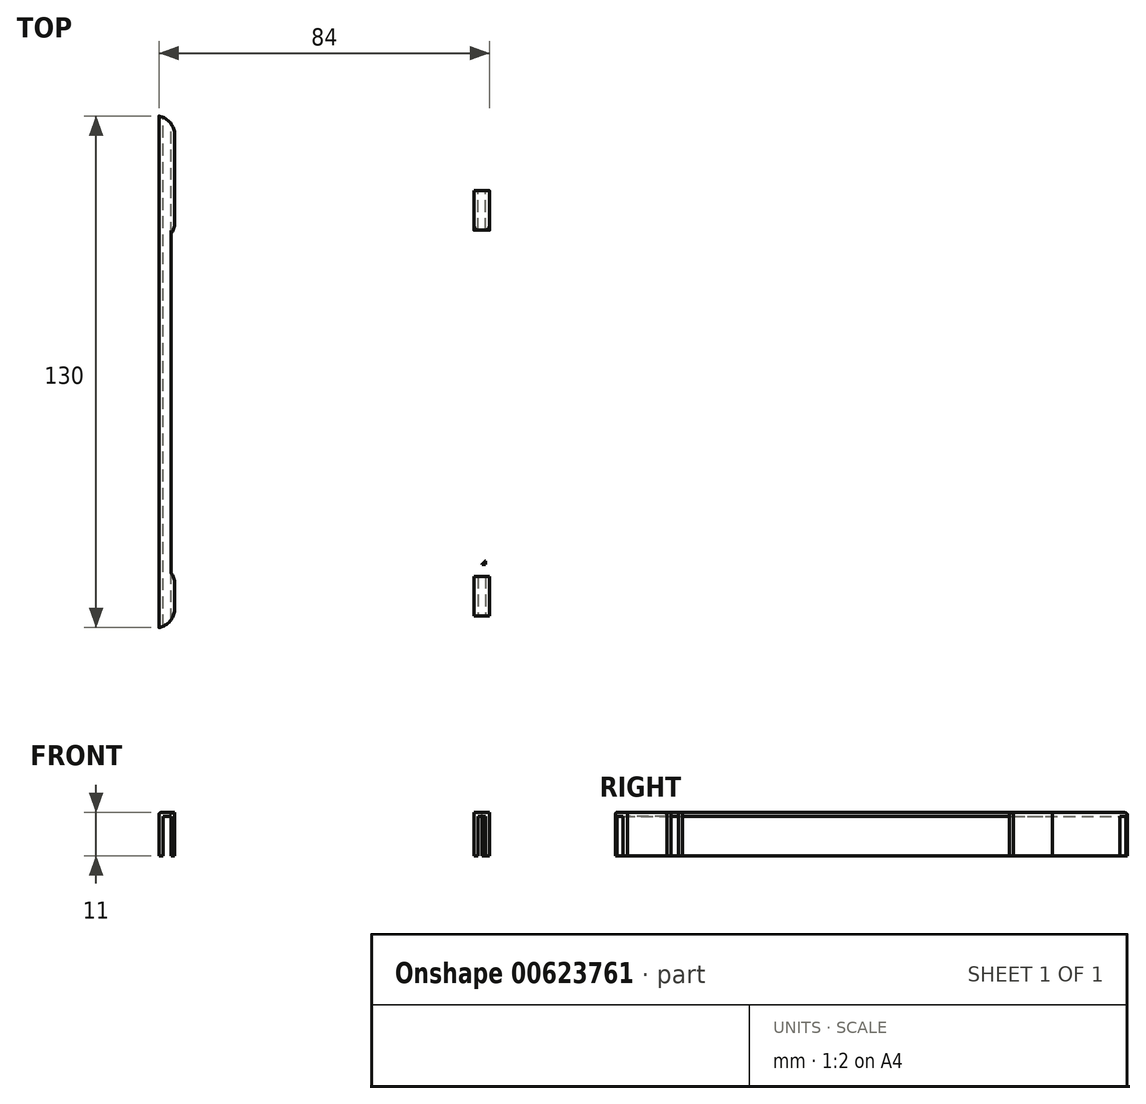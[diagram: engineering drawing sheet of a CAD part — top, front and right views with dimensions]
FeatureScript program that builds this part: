
annotation { "Feature Type Name" : "Feature", "Feature Type Description" : "" }
export const myFeature = defineFeature(function(context is Context, id is Id, definition is map)
    precondition{}
    {
        {
            var Q0;
            Q0=qCreatedBy(makeId("Top.planeOp"),FACE);
            var sketch = newSketch(context, id + "F0", { "sketchPlane" : qUnion([Q0])});
            skLineSegment(sketch, "E0.bottom", {"start": v(1, -65) * mm, "end": v(-1, -65) * mm});
            skLineSegment(sketch, "E0.top", {"start": v(1, 65) * mm, "end": v(-1, 65) * mm});
            skLineSegment(sketch, "E0.left", {"start": v(1, -65) * mm, "end": v(1, 65) * mm});
            skLineSegment(sketch, "E0.right", {"start": v(-1, -65) * mm, "end": v(-1, 65) * mm});
            skPoint(sketch, "E0.middle", {"position": v(0, 0) * mm});
            skLineSegment(sketch, "E1.bottom", {"start": v(1, -49) * mm, "end": v(120, -49) * mm});
            skLineSegment(sketch, "E1.top", {"start": v(1, -51) * mm, "end": v(120, -51) * mm});
            skLineSegment(sketch, "E1.left", {"start": v(1, -49) * mm, "end": v(1, -51) * mm});
            skLineSegment(sketch, "E1.right", {"start": v(120, -49) * mm, "end": v(120, -51) * mm});
            skLineSegment(sketch, "E2", {"start": v(1, -65) * mm, "end": v(1, -51) * mm});
            skLineSegment(sketch, "E3.bottom", {"start": v(1, 35) * mm, "end": v(120, 35) * mm});
            skLineSegment(sketch, "E3.top", {"start": v(1, 33) * mm, "end": v(120, 33) * mm});
            skLineSegment(sketch, "E3.left", {"start": v(1, 35) * mm, "end": v(1, 33) * mm});
            skLineSegment(sketch, "E3.right", {"start": v(120, 35) * mm, "end": v(120, 33) * mm});
            skLineSegment(sketch, "E4", {"start": v(1, 33) * mm, "end": v(1, -49) * mm});
            skLineSegment(sketch, "E5.bottom", {"start": v(-1, 65) * mm, "end": v(-2, 65) * mm});
            skLineSegment(sketch, "E5.top", {"start": v(-1, -65) * mm, "end": v(-2, -65) * mm});
            skLineSegment(sketch, "E5.left", {"start": v(-1, 65) * mm, "end": v(-1, -65) * mm});
            skLineSegment(sketch, "E5.right", {"start": v(-2, 65) * mm, "end": v(-2, -65) * mm});
            skLineSegment(sketch, "E6.bottom", {"start": v(1, 65) * mm, "end": v(2, 65) * mm});
            skLineSegment(sketch, "E6.top", {"start": v(1, 35) * mm, "end": v(2, 35) * mm});
            skLineSegment(sketch, "E6.left", {"start": v(1, 65) * mm, "end": v(1, 35) * mm});
            skLineSegment(sketch, "E6.right", {"start": v(2, 65) * mm, "end": v(2, 35) * mm});
            skLineSegment(sketch, "E7.bottom", {"start": v(1, 33) * mm, "end": v(2, 33) * mm});
            skLineSegment(sketch, "E7.top", {"start": v(1, -49) * mm, "end": v(2, -49) * mm});
            skLineSegment(sketch, "E7.right", {"start": v(2, 33) * mm, "end": v(2, -49) * mm});
            skLineSegment(sketch, "E8.bottom", {"start": v(1, -65) * mm, "end": v(2, -65) * mm});
            skLineSegment(sketch, "E8.top", {"start": v(1, -51) * mm, "end": v(2, -51) * mm});
            skLineSegment(sketch, "E8.right", {"start": v(2, -65) * mm, "end": v(2, -51) * mm});
            skLineSegment(sketch, "E9.bottom", {"start": v(2, 35) * mm, "end": v(79, 35) * mm});
            skLineSegment(sketch, "E9.top", {"start": v(2, 36) * mm, "end": v(79, 36) * mm});
            skLineSegment(sketch, "E9.left", {"start": v(2, 35) * mm, "end": v(2, 36) * mm});
            skLineSegment(sketch, "E9.right", {"start": v(79, 35) * mm, "end": v(79, 36) * mm});
            skLineSegment(sketch, "E10.bottom", {"start": v(2, 33) * mm, "end": v(79, 33) * mm});
            skLineSegment(sketch, "E10.top", {"start": v(2, 32) * mm, "end": v(79, 32) * mm});
            skLineSegment(sketch, "E10.left", {"start": v(2, 33) * mm, "end": v(2, 32) * mm});
            skLineSegment(sketch, "E10.right", {"start": v(79, 33) * mm, "end": v(79, 32) * mm});
            skLineSegment(sketch, "E11.bottom", {"start": v(2, -49) * mm, "end": v(79, -49) * mm});
            skLineSegment(sketch, "E11.top", {"start": v(2, -48) * mm, "end": v(79, -48) * mm});
            skLineSegment(sketch, "E11.left", {"start": v(2, -49) * mm, "end": v(2, -48) * mm});
            skLineSegment(sketch, "E11.right", {"start": v(79, -49) * mm, "end": v(79, -48) * mm});
            skLineSegment(sketch, "E12.bottom", {"start": v(2, -51) * mm, "end": v(79, -51) * mm});
            skLineSegment(sketch, "E12.top", {"start": v(2, -52) * mm, "end": v(79, -52) * mm});
            skLineSegment(sketch, "E12.left", {"start": v(2, -51) * mm, "end": v(2, -52) * mm});
            skLineSegment(sketch, "E12.right", {"start": v(79, -51) * mm, "end": v(79, -52) * mm});
            skLineSegment(sketch, "E13.bottom", {"start": v(79, 33) * mm, "end": v(81, 33) * mm});
            skLineSegment(sketch, "E13.top", {"start": v(79, 22) * mm, "end": v(81, 22) * mm});
            skLineSegment(sketch, "E13.left", {"start": v(79, 33) * mm, "end": v(79, 22) * mm});
            skLineSegment(sketch, "E13.right", {"start": v(81, 33) * mm, "end": v(81, 22) * mm});
            skLineSegment(sketch, "E14.bottom", {"start": v(79, -49) * mm, "end": v(81, -49) * mm});
            skLineSegment(sketch, "E14.top", {"start": v(79, -38) * mm, "end": v(81, -38) * mm});
            skLineSegment(sketch, "E14.left", {"start": v(79, -49) * mm, "end": v(79, -38) * mm});
            skLineSegment(sketch, "E14.right", {"start": v(81, -49) * mm, "end": v(81, -38) * mm});
            skLineSegment(sketch, "E15.bottom", {"start": v(79, 32) * mm, "end": v(78, 32) * mm});
            skLineSegment(sketch, "E15.top", {"start": v(79, 22) * mm, "end": v(78, 22) * mm});
            skLineSegment(sketch, "E15.left", {"start": v(79, 32) * mm, "end": v(79, 22) * mm});
            skLineSegment(sketch, "E15.right", {"start": v(78, 32) * mm, "end": v(78, 22) * mm});
            skLineSegment(sketch, "E16.bottom", {"start": v(79, -48) * mm, "end": v(78, -48) * mm});
            skLineSegment(sketch, "E16.top", {"start": v(79, -38) * mm, "end": v(78, -38) * mm});
            skLineSegment(sketch, "E16.left", {"start": v(79, -48) * mm, "end": v(79, -38) * mm});
            skLineSegment(sketch, "E16.right", {"start": v(78, -48) * mm, "end": v(78, -38) * mm});
            skLineSegment(sketch, "E17.bottom", {"start": v(81, -49) * mm, "end": v(120, -49) * mm});
            skLineSegment(sketch, "E17.top", {"start": v(81, -48) * mm, "end": v(120, -48) * mm});
            skLineSegment(sketch, "E17.left", {"start": v(81, -49) * mm, "end": v(81, -48) * mm});
            skLineSegment(sketch, "E17.right", {"start": v(120, -49) * mm, "end": v(120, -48) * mm});
            skLineSegment(sketch, "E18.bottom", {"start": v(81, 33) * mm, "end": v(120, 33) * mm});
            skLineSegment(sketch, "E18.top", {"start": v(81, 32) * mm, "end": v(120, 32) * mm});
            skLineSegment(sketch, "E18.left", {"start": v(81, 33) * mm, "end": v(81, 32) * mm});
            skLineSegment(sketch, "E18.right", {"start": v(120, 33) * mm, "end": v(120, 32) * mm});
            skLineSegment(sketch, "E19.bottom", {"start": v(81, 32) * mm, "end": v(82, 32) * mm});
            skLineSegment(sketch, "E19.top", {"start": v(81, 22) * mm, "end": v(82, 22) * mm});
            skLineSegment(sketch, "E19.left", {"start": v(81, 32) * mm, "end": v(81, 22) * mm});
            skLineSegment(sketch, "E19.right", {"start": v(82, 32) * mm, "end": v(82, 22) * mm});
            skLineSegment(sketch, "E20.bottom", {"start": v(81, -48) * mm, "end": v(82, -48) * mm});
            skLineSegment(sketch, "E20.top", {"start": v(81, -38) * mm, "end": v(82, -38) * mm});
            skLineSegment(sketch, "E20.left", {"start": v(81, -48) * mm, "end": v(81, -38) * mm});
            skLineSegment(sketch, "E20.right", {"start": v(82, -48) * mm, "end": v(82, -38) * mm});
            skLineSegment(sketch, "E21.bottom", {"start": v(79, -51) * mm, "end": v(120, -51) * mm});
            skLineSegment(sketch, "E21.top", {"start": v(79, -52) * mm, "end": v(120, -52) * mm});
            skLineSegment(sketch, "E21.right", {"start": v(120, -51) * mm, "end": v(120, -52) * mm});
            skLineSegment(sketch, "E22.bottom", {"start": v(79, 36) * mm, "end": v(120, 36) * mm});
            skLineSegment(sketch, "E22.top", {"start": v(79, 35) * mm, "end": v(120, 35) * mm});
            skLineSegment(sketch, "E22.left", {"start": v(79, 36) * mm, "end": v(79, 35) * mm});
            skLineSegment(sketch, "E22.right", {"start": v(120, 36) * mm, "end": v(120, 35) * mm});
            skLineSegment(sketch, "E23.bottom", {"start": v(-5.8, -72.8) * mm, "end": v(6.4, -72.8) * mm});
            skLineSegment(sketch, "E23.top", {"start": v(-5.8, -79.05) * mm, "end": v(6.4, -79.05) * mm});
            skLineSegment(sketch, "E23.left", {"start": v(-5.8, -72.8) * mm, "end": v(-5.8, -79.05) * mm});
            skLineSegment(sketch, "E23.right", {"start": v(6.4, -72.8) * mm, "end": v(6.4, -79.05) * mm});
            skLineSegment(sketch, "E24.bottom", {"start": v(79, 35) * mm, "end": v(81, 35) * mm});
            skLineSegment(sketch, "E24.top", {"start": v(79, 46) * mm, "end": v(81, 46) * mm});
            skLineSegment(sketch, "E24.left", {"start": v(79, 35) * mm, "end": v(79, 46) * mm});
            skLineSegment(sketch, "E24.right", {"start": v(81, 35) * mm, "end": v(81, 46) * mm});
            skLineSegment(sketch, "E25.bottom", {"start": v(81, 35) * mm, "end": v(82, 35) * mm});
            skLineSegment(sketch, "E25.top", {"start": v(81, 46) * mm, "end": v(82, 46) * mm});
            skLineSegment(sketch, "E25.right", {"start": v(82, 35) * mm, "end": v(82, 46) * mm});
            skLineSegment(sketch, "E26.bottom", {"start": v(79, 35) * mm, "end": v(78, 35) * mm});
            skLineSegment(sketch, "E26.top", {"start": v(79, 46) * mm, "end": v(78, 46) * mm});
            skLineSegment(sketch, "E26.right", {"start": v(78, 35) * mm, "end": v(78, 46) * mm});
            skLineSegment(sketch, "E27.bottom", {"start": v(79, -51) * mm, "end": v(78, -51) * mm});
            skLineSegment(sketch, "E27.top", {"start": v(79, -62) * mm, "end": v(78, -62) * mm});
            skLineSegment(sketch, "E27.left", {"start": v(79, -51) * mm, "end": v(79, -62) * mm});
            skLineSegment(sketch, "E27.right", {"start": v(78, -51) * mm, "end": v(78, -62) * mm});
            skLineSegment(sketch, "E28.bottom", {"start": v(79, -51) * mm, "end": v(81, -51) * mm});
            skLineSegment(sketch, "E28.top", {"start": v(79, -62) * mm, "end": v(81, -62) * mm});
            skLineSegment(sketch, "E28.right", {"start": v(81, -51) * mm, "end": v(81, -62) * mm});
            skLineSegment(sketch, "E29.bottom", {"start": v(81, -51) * mm, "end": v(82, -51) * mm});
            skLineSegment(sketch, "E29.top", {"start": v(81, -62) * mm, "end": v(82, -62) * mm});
            skLineSegment(sketch, "E29.right", {"start": v(82, -51) * mm, "end": v(82, -62) * mm});
            skLineSegment(sketch, "E30.top", {"start": v(79, 32) * mm, "end": v(81, 32) * mm});
            skLineSegment(sketch, "E31.bottom", {"start": v(79, -48) * mm, "end": v(81, -48) * mm});
            skLineSegment(sketch, "E31.left", {"start": v(79, -48) * mm, "end": v(79, -49) * mm});
            skLineSegment(sketch, "E31.right", {"start": v(81, -48) * mm, "end": v(81, -49) * mm});
            skSolve(sketch);
        }
        {
            var Q0;
            Q0=makeQuery(id+"F0.imprint","IMPRINT",FACE,{"disambiguationData":[TD([[makeQuery(id+"F0.imprint","IMPRINT",EDGE,{"derivedFrom":sQuery(id+"F0.wireOp",EDGE,"E0.bottom")}),-1.0]])]});
            var Q1;
            Q1=makeQuery(id+"F0.imprint","IMPRINT",FACE,{"disambiguationData":[TD([[makeQuery(id+"F0.imprint","IMPRINT",EDGE,{"derivedFrom":sQuery(id+"F0.wireOp",EDGE,"E3.left")}),1.0]])]});
            var Q2;
            {var subQ5=sQuery(id+"F0.wireOp",EDGE,"E24.top");Q2=makeQuery(id+"F0.imprint","IMPRINT",FACE,{"disambiguationData":[TD([[makeQuery(id+"F0.imprint","IMPRINT",EDGE,{"derivedFrom":subQ5}),-1.0]])]});}
            var Q3;
            {var subQ5=sQuery(id+"F0.wireOp",EDGE,"E24.bottom");Q3=makeQuery(id+"F0.imprint","IMPRINT",FACE,{"disambiguationData":[TD([[makeQuery(id+"F0.imprint","IMPRINT",EDGE,{"derivedFrom":subQ5}),1.0]])]});}
            var Q4;
            Q4=makeQuery(id+"F0.imprint","IMPRINT",FACE,{"disambiguationData":[TD([[makeQuery(id+"F0.imprint","IMPRINT",EDGE,{"derivedFrom":sQuery(id+"F0.wireOp",EDGE,"E1.left")}),1.0]])]});
            var Q5;
            {var subQ5=sQuery(id+"F0.wireOp",EDGE,"E28.top");Q5=makeQuery(id+"F0.imprint","IMPRINT",FACE,{"disambiguationData":[TD([[makeQuery(id+"F0.imprint","IMPRINT",EDGE,{"derivedFrom":subQ5}),1.0]])]});}
            var Q6;
            {var subQ5=sQuery(id+"F0.wireOp",EDGE,"E28.bottom");Q6=makeQuery(id+"F0.imprint","IMPRINT",FACE,{"disambiguationData":[TD([[makeQuery(id+"F0.imprint","IMPRINT",EDGE,{"derivedFrom":subQ5}),-1.0]])]});}
            extrude(context, id + "F1", {"entities" : qUnion([Q0, Q1, Q2, Q3, Q4, Q5, Q6]), "oppositeDirection" : true, "depth" : 0.9 * mm, "offsetDistance" : 25 * mm});
        }
        {
            var Q0;
            Q0=makeQuery(id+"F0.imprint","IMPRINT",FACE,{"disambiguationData":[TD([[makeQuery(id+"F0.imprint","IMPRINT",EDGE,{"derivedFrom":sQuery(id+"F0.wireOp",EDGE,"E6.bottom")}),-1.0]])]});
            var Q1;
            Q1=makeQuery(id+"F0.imprint","IMPRINT",FACE,{"disambiguationData":[TD([[makeQuery(id+"F0.imprint","IMPRINT",EDGE,{"derivedFrom":sQuery(id+"F0.wireOp",EDGE,"E5.bottom")}),1.0]])]});
            var Q2;
            {var subQ0=sQuery(id+"F0.wireOp",EDGE,"E9.bottom");Q2=makeQuery(id+"F0.imprint","IMPRINT",FACE,{"disambiguationData":[TD([[makeQuery(id+"F0.imprint","IMPRINT",EDGE,{"derivedFrom":subQ0}),1.0]])]});}
            var Q3;
            Q3=makeQuery(id+"F0.imprint","IMPRINT",FACE,{"disambiguationData":[TD([[makeQuery(id+"F0.imprint","IMPRINT",EDGE,{"derivedFrom":sQuery(id+"F0.wireOp",EDGE,"E10.bottom")}),-1.0]])]});
            var Q4;
            Q4=makeQuery(id+"F0.imprint","IMPRINT",FACE,{"disambiguationData":[TD([[makeQuery(id+"F0.imprint","IMPRINT",EDGE,{"derivedFrom":sQuery(id+"F0.wireOp",EDGE,"E7.bottom")}),-1.0]])]});
            var Q5;
            {var subQ5=sQuery(id+"F0.wireOp",EDGE,"E26.top");Q5=makeQuery(id+"F0.imprint","IMPRINT",FACE,{"disambiguationData":[TD([[makeQuery(id+"F0.imprint","IMPRINT",EDGE,{"derivedFrom":subQ5}),1.0]])]});}
            var Q6;
            {var subQ5=sQuery(id+"F0.wireOp",EDGE,"E25.top");Q6=makeQuery(id+"F0.imprint","IMPRINT",FACE,{"disambiguationData":[TD([[makeQuery(id+"F0.imprint","IMPRINT",EDGE,{"derivedFrom":subQ5}),-1.0]])]});}
            var Q7;
            {var subQ5=sQuery(id+"F0.wireOp",EDGE,"E25.bottom");Q7=makeQuery(id+"F0.imprint","IMPRINT",FACE,{"disambiguationData":[TD([[makeQuery(id+"F0.imprint","IMPRINT",EDGE,{"derivedFrom":subQ5}),1.0]])]});}
            var Q8;
            {var subQ5=sQuery(id+"F0.wireOp",EDGE,"E26.bottom");Q8=makeQuery(id+"F0.imprint","IMPRINT",FACE,{"disambiguationData":[TD([[makeQuery(id+"F0.imprint","IMPRINT",EDGE,{"derivedFrom":subQ5}),-1.0]])]});}
            var Q9;
            {var subQ4=sQuery(id+"F0.wireOp",EDGE,"E22.top");Q9=makeQuery(id+"F0.imprint","IMPRINT",FACE,{"disambiguationData":[TD([[makeQuery(id+"F0.imprint","IMPRINT",EDGE,{"derivedFrom":subQ4}),1.0]])]});}
            var Q10;
            Q10=makeQuery(id+"F0.imprint","IMPRINT",FACE,{"disambiguationData":[TD([[makeQuery(id+"F0.imprint","IMPRINT",EDGE,{"derivedFrom":sQuery(id+"F0.wireOp",EDGE,"E18.bottom")}),-1.0]])]});
            var Q11;
            Q11=makeQuery(id+"F0.imprint","IMPRINT",FACE,{"disambiguationData":[TD([[makeQuery(id+"F0.imprint","IMPRINT",EDGE,{"derivedFrom":sQuery(id+"F0.wireOp",EDGE,"E13.bottom")}),-1.0]])]});
            var Q12;
            Q12=makeQuery(id+"F0.imprint","IMPRINT",FACE,{"disambiguationData":[TD([[makeQuery(id+"F0.imprint","IMPRINT",EDGE,{"derivedFrom":sQuery(id+"F0.wireOp",EDGE,"E11.bottom")}),1.0]])]});
            var Q13;
            {var subQ0=sQuery(id+"F0.wireOp",EDGE,"E12.bottom");Q13=makeQuery(id+"F0.imprint","IMPRINT",FACE,{"disambiguationData":[TD([[makeQuery(id+"F0.imprint","IMPRINT",EDGE,{"derivedFrom":subQ0}),-1.0]])]});}
            var Q14;
            Q14=makeQuery(id+"F0.imprint","IMPRINT",FACE,{"disambiguationData":[TD([[makeQuery(id+"F0.imprint","IMPRINT",EDGE,{"derivedFrom":sQuery(id+"F0.wireOp",EDGE,"E8.bottom")}),1.0]])]});
            var Q15;
            Q15=makeQuery(id+"F0.imprint","IMPRINT",FACE,{"disambiguationData":[TD([[makeQuery(id+"F0.imprint","IMPRINT",EDGE,{"derivedFrom":sQuery(id+"F0.wireOp",EDGE,"E17.bottom")}),1.0]])]});
            var Q16;
            Q16=makeQuery(id+"F0.imprint","IMPRINT",FACE,{"disambiguationData":[TD([[makeQuery(id+"F0.imprint","IMPRINT",EDGE,{"derivedFrom":sQuery(id+"F0.wireOp",EDGE,"E31.bottom")}),-1.0]])]});
            var Q17;
            {var subQ5=sQuery(id+"F0.wireOp",EDGE,"E27.top");Q17=makeQuery(id+"F0.imprint","IMPRINT",FACE,{"disambiguationData":[TD([[makeQuery(id+"F0.imprint","IMPRINT",EDGE,{"derivedFrom":subQ5}),-1.0]])]});}
            var Q18;
            {var subQ5=sQuery(id+"F0.wireOp",EDGE,"E27.bottom");Q18=makeQuery(id+"F0.imprint","IMPRINT",FACE,{"disambiguationData":[TD([[makeQuery(id+"F0.imprint","IMPRINT",EDGE,{"derivedFrom":subQ5}),1.0]])]});}
            var Q19;
            {var subQ0=sQuery(id+"F0.wireOp",EDGE,"E21.bottom");Q19=makeQuery(id+"F0.imprint","IMPRINT",FACE,{"disambiguationData":[TD([[makeQuery(id+"F0.imprint","IMPRINT",EDGE,{"derivedFrom":subQ0}),-1.0]])]});}
            var Q20;
            {var subQ5=sQuery(id+"F0.wireOp",EDGE,"E29.bottom");Q20=makeQuery(id+"F0.imprint","IMPRINT",FACE,{"disambiguationData":[TD([[makeQuery(id+"F0.imprint","IMPRINT",EDGE,{"derivedFrom":subQ5}),-1.0]])]});}
            var Q21;
            {var subQ5=sQuery(id+"F0.wireOp",EDGE,"E29.top");Q21=makeQuery(id+"F0.imprint","IMPRINT",FACE,{"disambiguationData":[TD([[makeQuery(id+"F0.imprint","IMPRINT",EDGE,{"derivedFrom":subQ5}),1.0]])]});}
            extrude(context, id + "F2", {"entities" : qUnion([Q0, Q1, Q2, Q3, Q4, Q5, Q6, Q7, Q8, Q9, Q10, Q11, Q12, Q13, Q14, Q15, Q16, Q17, Q18, Q19, Q20, Q21]), "operationType" : NewBodyOperationType.ADD, "oppositeDirection" : true, "depth" : 11 * mm, "offsetDistance" : 25 * mm});
        }
        {
            var Q0;
            Q0=makeQuery(id+"F2.opExtrude","SWEPT_EDGE",EDGE,{"disambiguationData":[OSD([sQuery(id+"F0.wireOp",EDGE,"E12.top"),sQuery(id+"F0.wireOp",EDGE,"E27.right")])]});
            var Q1;
            Q1=makeQuery(id+"F2.opExtrude","SWEPT_EDGE",EDGE,{"disambiguationData":[OSD([sQuery(id+"F0.wireOp",EDGE,"E28.bottom"),sQuery(id+"F0.wireOp",EDGE,"E29.bottom"),sQuery(id+"F0.wireOp",EDGE,"E28.right")])]});
            var Q2;
            Q2=makeQuery(id+"F2.opExtrude","SWEPT_EDGE",EDGE,{"disambiguationData":[OSD([sQuery(id+"F0.wireOp",EDGE,"E21.top"),sQuery(id+"F0.wireOp",EDGE,"E29.right")])]});
            var Q3;
            Q3=makeQuery(id+"F2.opExtrude","SWEPT_EDGE",EDGE,{"disambiguationData":[OSD([sQuery(id+"F0.wireOp",EDGE,"E27.bottom"),sQuery(id+"F0.wireOp",EDGE,"E28.bottom"),sQuery(id+"F0.wireOp",EDGE,"E27.left")])]});
            var Q4;
            Q4=makeQuery(id+"F2.opExtrude","SWEPT_EDGE",EDGE,{"disambiguationData":[OSD([sQuery(id+"F0.wireOp",EDGE,"E1.left"),sQuery(id+"F0.wireOp",EDGE,"E7.top"),sQuery(id+"F0.wireOp",EDGE,"E4")])]});
            var Q5;
            Q5=makeQuery(id+"F2.opExtrude","SWEPT_EDGE",EDGE,{"disambiguationData":[OSD([sQuery(id+"F0.wireOp",EDGE,"E1.left"),sQuery(id+"F0.wireOp",EDGE,"E8.top"),sQuery(id+"F0.wireOp",EDGE,"E2")])]});
            var Q6;
            Q6=makeQuery(id+"F2.opExtrude","SWEPT_EDGE",EDGE,{"disambiguationData":[OSD([sQuery(id+"F0.wireOp",EDGE,"E8.right"),sQuery(id+"F0.wireOp",EDGE,"E12.top"),sQuery(id+"F0.wireOp",EDGE,"E12.left")])]});
            var Q7;
            Q7=makeQuery(id+"F2.opExtrude","SWEPT_EDGE",EDGE,{"disambiguationData":[OSD([sQuery(id+"F0.wireOp",EDGE,"E7.right"),sQuery(id+"F0.wireOp",EDGE,"E11.top"),sQuery(id+"F0.wireOp",EDGE,"E11.left")])]});
            var Q8;
            Q8=makeQuery(id+"F2.opExtrude","SWEPT_EDGE",EDGE,{"disambiguationData":[OSD([sQuery(id+"F0.wireOp",EDGE,"E6.right"),sQuery(id+"F0.wireOp",EDGE,"E9.top"),sQuery(id+"F0.wireOp",EDGE,"E9.left")])]});
            var Q9;
            Q9=makeQuery(id+"F2.opExtrude","SWEPT_EDGE",EDGE,{"disambiguationData":[OSD([sQuery(id+"F0.wireOp",EDGE,"E3.left"),sQuery(id+"F0.wireOp",EDGE,"E7.bottom"),sQuery(id+"F0.wireOp",EDGE,"E4")])]});
            var Q10;
            Q10=makeQuery(id+"F2.opExtrude","SWEPT_EDGE",EDGE,{"disambiguationData":[OSD([sQuery(id+"F0.wireOp",EDGE,"E3.left"),sQuery(id+"F0.wireOp",EDGE,"E6.top"),sQuery(id+"F0.wireOp",EDGE,"E6.left")])]});
            var Q11;
            Q11=makeQuery(id+"F2.opExtrude","SWEPT_EDGE",EDGE,{"disambiguationData":[OSD([sQuery(id+"F0.wireOp",EDGE,"E7.right"),sQuery(id+"F0.wireOp",EDGE,"E10.top"),sQuery(id+"F0.wireOp",EDGE,"E10.left")])]});
            var Q12;
            Q12=makeQuery(id+"F2.opExtrude","SWEPT_EDGE",EDGE,{"disambiguationData":[OSD([sQuery(id+"F0.wireOp",EDGE,"E24.bottom"),sQuery(id+"F0.wireOp",EDGE,"E25.bottom"),sQuery(id+"F0.wireOp",EDGE,"E24.right")])]});
            var Q13;
            Q13=makeQuery(id+"F2.opExtrude","SWEPT_EDGE",EDGE,{"disambiguationData":[OSD([sQuery(id+"F0.wireOp",EDGE,"E24.bottom"),sQuery(id+"F0.wireOp",EDGE,"E26.bottom"),sQuery(id+"F0.wireOp",EDGE,"E24.left")])]});
            var Q14;
            Q14=makeQuery(id+"F2.opExtrude","SWEPT_EDGE",EDGE,{"disambiguationData":[OSD([sQuery(id+"F0.wireOp",EDGE,"E22.bottom"),sQuery(id+"F0.wireOp",EDGE,"E25.right")])]});
            var Q15;
            Q15=makeQuery(id+"F2.opExtrude","SWEPT_EDGE",EDGE,{"disambiguationData":[OSD([sQuery(id+"F0.wireOp",EDGE,"E9.top"),sQuery(id+"F0.wireOp",EDGE,"E26.right")])]});
            fillet(context, id + "F3", {"entities" : qUnion([Q0, Q1, Q2, Q3, Q4, Q5, Q6, Q7, Q8, Q9, Q10, Q11, Q12, Q13, Q14, Q15]), "radius" : 5 * mm, "tangentPropagation" : true, "allowEdgeOverflow" : false});
        }
        {
            var Q0;
            Q0=makeQuery(id+"F2.opExtrude","CAP_EDGE",EDGE,{"disambiguationData":[OSD([sQuery(id+"F0.wireOp",EDGE,"E10.top"),sQuery(id+"F0.wireOp",EDGE,"E15.bottom"),sQuery(id+"F0.wireOp",EDGE,"E18.top"),sQuery(id+"F0.wireOp",EDGE,"E19.bottom"),sQuery(id+"F0.wireOp",EDGE,"E30.top")])],"isStart":true});
            var Q1;
            Q1=makeQuery(id+"F2.opExtrude","CAP_EDGE",EDGE,{"disambiguationData":[OSD([sQuery(id+"F0.wireOp",EDGE,"E22.bottom")])],"isStart":true});
            var Q2;
            {var subQ0=sQuery(id+"F0.wireOp",EDGE,"E25.right");var subQ1=sQuery(id+"F0.wireOp",EDGE,"E24.right");var subQ2=sQuery(id+"F0.wireOp",EDGE,"E25.bottom");var subQ3=sQuery(id+"F0.wireOp",EDGE,"E22.top");var subQ4=sQuery(id+"F0.wireOp",EDGE,"E22.bottom");var subQ5=sQuery(id+"F0.wireOp",EDGE,"E28.right");var subQ6=sQuery(id+"F0.wireOp",EDGE,"E29.bottom");var subQ7=sQuery(id+"F0.wireOp",EDGE,"E21.bottom");var subQ8=sQuery(id+"F0.wireOp",EDGE,"E27.left");var subQ9=sQuery(id+"F0.wireOp",EDGE,"E27.bottom");var subQ10=sQuery(id+"F0.wireOp",EDGE,"E12.bottom");var subQ11=sQuery(id+"F0.wireOp",EDGE,"E2");var subQ12=sQuery(id+"F0.wireOp",EDGE,"E8.top");var subQ13=sQuery(id+"F0.wireOp",EDGE,"E14.bottom");var subQ14=sQuery(id+"F0.wireOp",EDGE,"E13.bottom");var subQ15=sQuery(id+"F0.wireOp",EDGE,"E18.bottom");var subQ16=sQuery(id+"F0.wireOp",EDGE,"E17.bottom");var subQ17=sQuery(id+"F0.wireOp",EDGE,"E11.bottom");var subQ18=sQuery(id+"F0.wireOp",EDGE,"E10.bottom");var subQ19=sQuery(id+"F0.wireOp",EDGE,"E4");var subQ20=sQuery(id+"F0.wireOp",EDGE,"E7.top");var subQ21=sQuery(id+"F0.wireOp",EDGE,"E7.bottom");var subQ22=sQuery(id+"F0.wireOp",EDGE,"E24.left");var subQ23=sQuery(id+"F0.wireOp",EDGE,"E26.bottom");var subQ24=sQuery(id+"F0.wireOp",EDGE,"E9.bottom");var subQ25=sQuery(id+"F0.wireOp",EDGE,"E6.left");var subQ26=sQuery(id+"F0.wireOp",EDGE,"E6.top");var subQ27=sQuery(id+"F0.wireOp",EDGE,"E5.left");Q2=makeQuery(id+"F3.opFillet","BLEND_EDGE",EDGE,{"blendedFrom":[makeQuery(id+"F2.opExtrude","SWEPT_EDGE",EDGE,{"disambiguationData":[OSD([subQ4,subQ0])]}),makeQuery(id+"F2.boolean.opBoolean","MERGE",FACE,{"derivedFrom":[makeQuery(id+"F1.opExtrude","CAP_FACE",FACE,{"disambiguationData":[OSD([sQuery(id+"F0.wireOp",EDGE,"E0.bottom"),sQuery(id+"F0.wireOp",EDGE,"E0.top"),sQuery(id+"F0.wireOp",EDGE,"E1.right"),sQuery(id+"F0.wireOp",EDGE,"E3.right"),subQ27,subQ26,subQ25,subQ21,subQ20,subQ19,subQ12,subQ11,subQ24,subQ18,subQ17,subQ10,subQ16,subQ15,subQ7,subQ3,sQuery(id+"F0.wireOp",EDGE,"E24.top"),subQ2,subQ1,subQ23,subQ22,subQ9,sQuery(id+"F0.wireOp",EDGE,"E28.top"),subQ8,subQ6,subQ5,subQ14,subQ13])],"isStart":true}),makeQuery(id+"F2.opExtrude","CAP_FACE",FACE,{"disambiguationData":[OSD([sQuery(id+"F0.wireOp",EDGE,"E5.bottom"),sQuery(id+"F0.wireOp",EDGE,"E5.top"),subQ27,sQuery(id+"F0.wireOp",EDGE,"E5.right")])],"isStart":true}),makeQuery(id+"F2.opExtrude","CAP_FACE",FACE,{"disambiguationData":[OSD([sQuery(id+"F0.wireOp",EDGE,"E6.bottom"),subQ26,subQ25,sQuery(id+"F0.wireOp",EDGE,"E6.right"),subQ24,sQuery(id+"F0.wireOp",EDGE,"E9.top"),subQ23,sQuery(id+"F0.wireOp",EDGE,"E26.top"),subQ22,sQuery(id+"F0.wireOp",EDGE,"E26.right")])],"isStart":true}),makeQuery(id+"F2.opExtrude","CAP_FACE",FACE,{"disambiguationData":[OSD([subQ21,subQ20,subQ19,sQuery(id+"F0.wireOp",EDGE,"E7.right"),subQ18,sQuery(id+"F0.wireOp",EDGE,"E10.top"),subQ17,sQuery(id+"F0.wireOp",EDGE,"E11.top"),sQuery(id+"F0.wireOp",EDGE,"E15.bottom"),sQuery(id+"F0.wireOp",EDGE,"E16.bottom"),subQ16,sQuery(id+"F0.wireOp",EDGE,"E17.top"),sQuery(id+"F0.wireOp",EDGE,"E17.right"),subQ15,sQuery(id+"F0.wireOp",EDGE,"E18.top"),sQuery(id+"F0.wireOp",EDGE,"E18.right"),sQuery(id+"F0.wireOp",EDGE,"E19.bottom"),sQuery(id+"F0.wireOp",EDGE,"E20.bottom"),subQ14,sQuery(id+"F0.wireOp",EDGE,"E30.top"),sQuery(id+"F0.wireOp",EDGE,"E31.bottom"),subQ13])],"isStart":true}),makeQuery(id+"F2.opExtrude","CAP_FACE",FACE,{"disambiguationData":[OSD([sQuery(id+"F0.wireOp",EDGE,"E8.bottom"),subQ12,subQ11,sQuery(id+"F0.wireOp",EDGE,"E8.right"),subQ10,sQuery(id+"F0.wireOp",EDGE,"E12.top"),subQ9,sQuery(id+"F0.wireOp",EDGE,"E27.top"),sQuery(id+"F0.wireOp",EDGE,"E27.right"),subQ8])],"isStart":true}),makeQuery(id+"F2.opExtrude","CAP_FACE",FACE,{"disambiguationData":[OSD([subQ7,sQuery(id+"F0.wireOp",EDGE,"E21.top"),sQuery(id+"F0.wireOp",EDGE,"E21.right"),subQ6,sQuery(id+"F0.wireOp",EDGE,"E29.top"),subQ5,sQuery(id+"F0.wireOp",EDGE,"E29.right")])],"isStart":true}),makeQuery(id+"F2.opExtrude","CAP_FACE",FACE,{"disambiguationData":[OSD([subQ4,subQ3,sQuery(id+"F0.wireOp",EDGE,"E22.right"),subQ2,sQuery(id+"F0.wireOp",EDGE,"E25.top"),subQ1,subQ0])],"isStart":true})]})],"blendedInto":[makeQuery(id+"F2.boolean.opBoolean","MERGE",FACE,{"derivedFrom":[makeQuery(id+"F1.opExtrude","CAP_FACE",FACE,{"disambiguationData":[OSD([sQuery(id+"F0.wireOp",EDGE,"E0.bottom"),sQuery(id+"F0.wireOp",EDGE,"E0.top"),sQuery(id+"F0.wireOp",EDGE,"E1.right"),sQuery(id+"F0.wireOp",EDGE,"E3.right"),subQ27,subQ26,subQ25,subQ21,subQ20,subQ19,subQ12,subQ11,subQ24,subQ18,subQ17,subQ10,subQ16,subQ15,subQ7,subQ3,sQuery(id+"F0.wireOp",EDGE,"E24.top"),subQ2,subQ1,subQ23,subQ22,subQ9,sQuery(id+"F0.wireOp",EDGE,"E28.top"),subQ8,subQ6,subQ5,subQ14,subQ13])],"isStart":true}),makeQuery(id+"F2.opExtrude","CAP_FACE",FACE,{"disambiguationData":[OSD([sQuery(id+"F0.wireOp",EDGE,"E5.bottom"),sQuery(id+"F0.wireOp",EDGE,"E5.top"),subQ27,sQuery(id+"F0.wireOp",EDGE,"E5.right")])],"isStart":true}),makeQuery(id+"F2.opExtrude","CAP_FACE",FACE,{"disambiguationData":[OSD([sQuery(id+"F0.wireOp",EDGE,"E6.bottom"),subQ26,subQ25,sQuery(id+"F0.wireOp",EDGE,"E6.right"),subQ24,sQuery(id+"F0.wireOp",EDGE,"E9.top"),subQ23,sQuery(id+"F0.wireOp",EDGE,"E26.top"),subQ22,sQuery(id+"F0.wireOp",EDGE,"E26.right")])],"isStart":true}),makeQuery(id+"F2.opExtrude","CAP_FACE",FACE,{"disambiguationData":[OSD([subQ21,subQ20,subQ19,sQuery(id+"F0.wireOp",EDGE,"E7.right"),subQ18,sQuery(id+"F0.wireOp",EDGE,"E10.top"),subQ17,sQuery(id+"F0.wireOp",EDGE,"E11.top"),sQuery(id+"F0.wireOp",EDGE,"E15.bottom"),sQuery(id+"F0.wireOp",EDGE,"E16.bottom"),subQ16,sQuery(id+"F0.wireOp",EDGE,"E17.top"),sQuery(id+"F0.wireOp",EDGE,"E17.right"),subQ15,sQuery(id+"F0.wireOp",EDGE,"E18.top"),sQuery(id+"F0.wireOp",EDGE,"E18.right"),sQuery(id+"F0.wireOp",EDGE,"E19.bottom"),sQuery(id+"F0.wireOp",EDGE,"E20.bottom"),subQ14,sQuery(id+"F0.wireOp",EDGE,"E30.top"),sQuery(id+"F0.wireOp",EDGE,"E31.bottom"),subQ13])],"isStart":true}),makeQuery(id+"F2.opExtrude","CAP_FACE",FACE,{"disambiguationData":[OSD([sQuery(id+"F0.wireOp",EDGE,"E8.bottom"),subQ12,subQ11,sQuery(id+"F0.wireOp",EDGE,"E8.right"),subQ10,sQuery(id+"F0.wireOp",EDGE,"E12.top"),subQ9,sQuery(id+"F0.wireOp",EDGE,"E27.top"),sQuery(id+"F0.wireOp",EDGE,"E27.right"),subQ8])],"isStart":true}),makeQuery(id+"F2.opExtrude","CAP_FACE",FACE,{"disambiguationData":[OSD([subQ7,sQuery(id+"F0.wireOp",EDGE,"E21.top"),sQuery(id+"F0.wireOp",EDGE,"E21.right"),subQ6,sQuery(id+"F0.wireOp",EDGE,"E29.top"),subQ5,sQuery(id+"F0.wireOp",EDGE,"E29.right")])],"isStart":true}),makeQuery(id+"F2.opExtrude","CAP_FACE",FACE,{"disambiguationData":[OSD([subQ4,subQ3,sQuery(id+"F0.wireOp",EDGE,"E22.right"),subQ2,sQuery(id+"F0.wireOp",EDGE,"E25.top"),subQ1,subQ0])],"isStart":true})]})]});}
            var Q3;
            Q3=makeQuery(id+"F2.opExtrude","CAP_EDGE",EDGE,{"disambiguationData":[OSD([sQuery(id+"F0.wireOp",EDGE,"E25.right")])],"isStart":true});
            var Q4;
            Q4=makeQuery(id+"F2.opExtrude","CAP_EDGE",EDGE,{"disambiguationData":[OSD([sQuery(id+"F0.wireOp",EDGE,"E26.right")])],"isStart":true});
            var Q5;
            {var subQ0=sQuery(id+"F0.wireOp",EDGE,"E24.right");var subQ1=sQuery(id+"F0.wireOp",EDGE,"E25.bottom");var subQ2=sQuery(id+"F0.wireOp",EDGE,"E22.top");var subQ3=sQuery(id+"F0.wireOp",EDGE,"E28.right");var subQ4=sQuery(id+"F0.wireOp",EDGE,"E29.bottom");var subQ5=sQuery(id+"F0.wireOp",EDGE,"E21.bottom");var subQ6=sQuery(id+"F0.wireOp",EDGE,"E27.left");var subQ7=sQuery(id+"F0.wireOp",EDGE,"E27.bottom");var subQ8=sQuery(id+"F0.wireOp",EDGE,"E12.bottom");var subQ9=sQuery(id+"F0.wireOp",EDGE,"E2");var subQ10=sQuery(id+"F0.wireOp",EDGE,"E8.top");var subQ11=sQuery(id+"F0.wireOp",EDGE,"E14.bottom");var subQ12=sQuery(id+"F0.wireOp",EDGE,"E13.bottom");var subQ13=sQuery(id+"F0.wireOp",EDGE,"E18.bottom");var subQ14=sQuery(id+"F0.wireOp",EDGE,"E17.bottom");var subQ15=sQuery(id+"F0.wireOp",EDGE,"E11.bottom");var subQ16=sQuery(id+"F0.wireOp",EDGE,"E10.bottom");var subQ17=sQuery(id+"F0.wireOp",EDGE,"E4");var subQ18=sQuery(id+"F0.wireOp",EDGE,"E7.top");var subQ19=sQuery(id+"F0.wireOp",EDGE,"E7.bottom");var subQ20=sQuery(id+"F0.wireOp",EDGE,"E26.right");var subQ21=sQuery(id+"F0.wireOp",EDGE,"E24.left");var subQ22=sQuery(id+"F0.wireOp",EDGE,"E26.bottom");var subQ23=sQuery(id+"F0.wireOp",EDGE,"E9.top");var subQ24=sQuery(id+"F0.wireOp",EDGE,"E9.bottom");var subQ25=sQuery(id+"F0.wireOp",EDGE,"E6.left");var subQ26=sQuery(id+"F0.wireOp",EDGE,"E6.top");var subQ27=sQuery(id+"F0.wireOp",EDGE,"E5.left");Q5=makeQuery(id+"F3.opFillet","BLEND_EDGE",EDGE,{"blendedFrom":[makeQuery(id+"F2.opExtrude","SWEPT_EDGE",EDGE,{"disambiguationData":[OSD([subQ23,subQ20])]}),makeQuery(id+"F2.boolean.opBoolean","MERGE",FACE,{"derivedFrom":[makeQuery(id+"F1.opExtrude","CAP_FACE",FACE,{"disambiguationData":[OSD([sQuery(id+"F0.wireOp",EDGE,"E0.bottom"),sQuery(id+"F0.wireOp",EDGE,"E0.top"),sQuery(id+"F0.wireOp",EDGE,"E1.right"),sQuery(id+"F0.wireOp",EDGE,"E3.right"),subQ27,subQ26,subQ25,subQ19,subQ18,subQ17,subQ10,subQ9,subQ24,subQ16,subQ15,subQ8,subQ14,subQ13,subQ5,subQ2,sQuery(id+"F0.wireOp",EDGE,"E24.top"),subQ1,subQ0,subQ22,subQ21,subQ7,sQuery(id+"F0.wireOp",EDGE,"E28.top"),subQ6,subQ4,subQ3,subQ12,subQ11])],"isStart":true}),makeQuery(id+"F2.opExtrude","CAP_FACE",FACE,{"disambiguationData":[OSD([sQuery(id+"F0.wireOp",EDGE,"E5.bottom"),sQuery(id+"F0.wireOp",EDGE,"E5.top"),subQ27,sQuery(id+"F0.wireOp",EDGE,"E5.right")])],"isStart":true}),makeQuery(id+"F2.opExtrude","CAP_FACE",FACE,{"disambiguationData":[OSD([sQuery(id+"F0.wireOp",EDGE,"E6.bottom"),subQ26,subQ25,sQuery(id+"F0.wireOp",EDGE,"E6.right"),subQ24,subQ23,subQ22,sQuery(id+"F0.wireOp",EDGE,"E26.top"),subQ21,subQ20])],"isStart":true}),makeQuery(id+"F2.opExtrude","CAP_FACE",FACE,{"disambiguationData":[OSD([subQ19,subQ18,subQ17,sQuery(id+"F0.wireOp",EDGE,"E7.right"),subQ16,sQuery(id+"F0.wireOp",EDGE,"E10.top"),subQ15,sQuery(id+"F0.wireOp",EDGE,"E11.top"),sQuery(id+"F0.wireOp",EDGE,"E15.bottom"),sQuery(id+"F0.wireOp",EDGE,"E16.bottom"),subQ14,sQuery(id+"F0.wireOp",EDGE,"E17.top"),sQuery(id+"F0.wireOp",EDGE,"E17.right"),subQ13,sQuery(id+"F0.wireOp",EDGE,"E18.top"),sQuery(id+"F0.wireOp",EDGE,"E18.right"),sQuery(id+"F0.wireOp",EDGE,"E19.bottom"),sQuery(id+"F0.wireOp",EDGE,"E20.bottom"),subQ12,sQuery(id+"F0.wireOp",EDGE,"E30.top"),sQuery(id+"F0.wireOp",EDGE,"E31.bottom"),subQ11])],"isStart":true}),makeQuery(id+"F2.opExtrude","CAP_FACE",FACE,{"disambiguationData":[OSD([sQuery(id+"F0.wireOp",EDGE,"E8.bottom"),subQ10,subQ9,sQuery(id+"F0.wireOp",EDGE,"E8.right"),subQ8,sQuery(id+"F0.wireOp",EDGE,"E12.top"),subQ7,sQuery(id+"F0.wireOp",EDGE,"E27.top"),sQuery(id+"F0.wireOp",EDGE,"E27.right"),subQ6])],"isStart":true}),makeQuery(id+"F2.opExtrude","CAP_FACE",FACE,{"disambiguationData":[OSD([subQ5,sQuery(id+"F0.wireOp",EDGE,"E21.top"),sQuery(id+"F0.wireOp",EDGE,"E21.right"),subQ4,sQuery(id+"F0.wireOp",EDGE,"E29.top"),subQ3,sQuery(id+"F0.wireOp",EDGE,"E29.right")])],"isStart":true}),makeQuery(id+"F2.opExtrude","CAP_FACE",FACE,{"disambiguationData":[OSD([sQuery(id+"F0.wireOp",EDGE,"E22.bottom"),subQ2,sQuery(id+"F0.wireOp",EDGE,"E22.right"),subQ1,sQuery(id+"F0.wireOp",EDGE,"E25.top"),subQ0,sQuery(id+"F0.wireOp",EDGE,"E25.right")])],"isStart":true})]})],"blendedInto":[makeQuery(id+"F2.boolean.opBoolean","MERGE",FACE,{"derivedFrom":[makeQuery(id+"F1.opExtrude","CAP_FACE",FACE,{"disambiguationData":[OSD([sQuery(id+"F0.wireOp",EDGE,"E0.bottom"),sQuery(id+"F0.wireOp",EDGE,"E0.top"),sQuery(id+"F0.wireOp",EDGE,"E1.right"),sQuery(id+"F0.wireOp",EDGE,"E3.right"),subQ27,subQ26,subQ25,subQ19,subQ18,subQ17,subQ10,subQ9,subQ24,subQ16,subQ15,subQ8,subQ14,subQ13,subQ5,subQ2,sQuery(id+"F0.wireOp",EDGE,"E24.top"),subQ1,subQ0,subQ22,subQ21,subQ7,sQuery(id+"F0.wireOp",EDGE,"E28.top"),subQ6,subQ4,subQ3,subQ12,subQ11])],"isStart":true}),makeQuery(id+"F2.opExtrude","CAP_FACE",FACE,{"disambiguationData":[OSD([sQuery(id+"F0.wireOp",EDGE,"E5.bottom"),sQuery(id+"F0.wireOp",EDGE,"E5.top"),subQ27,sQuery(id+"F0.wireOp",EDGE,"E5.right")])],"isStart":true}),makeQuery(id+"F2.opExtrude","CAP_FACE",FACE,{"disambiguationData":[OSD([sQuery(id+"F0.wireOp",EDGE,"E6.bottom"),subQ26,subQ25,sQuery(id+"F0.wireOp",EDGE,"E6.right"),subQ24,subQ23,subQ22,sQuery(id+"F0.wireOp",EDGE,"E26.top"),subQ21,subQ20])],"isStart":true}),makeQuery(id+"F2.opExtrude","CAP_FACE",FACE,{"disambiguationData":[OSD([subQ19,subQ18,subQ17,sQuery(id+"F0.wireOp",EDGE,"E7.right"),subQ16,sQuery(id+"F0.wireOp",EDGE,"E10.top"),subQ15,sQuery(id+"F0.wireOp",EDGE,"E11.top"),sQuery(id+"F0.wireOp",EDGE,"E15.bottom"),sQuery(id+"F0.wireOp",EDGE,"E16.bottom"),subQ14,sQuery(id+"F0.wireOp",EDGE,"E17.top"),sQuery(id+"F0.wireOp",EDGE,"E17.right"),subQ13,sQuery(id+"F0.wireOp",EDGE,"E18.top"),sQuery(id+"F0.wireOp",EDGE,"E18.right"),sQuery(id+"F0.wireOp",EDGE,"E19.bottom"),sQuery(id+"F0.wireOp",EDGE,"E20.bottom"),subQ12,sQuery(id+"F0.wireOp",EDGE,"E30.top"),sQuery(id+"F0.wireOp",EDGE,"E31.bottom"),subQ11])],"isStart":true}),makeQuery(id+"F2.opExtrude","CAP_FACE",FACE,{"disambiguationData":[OSD([sQuery(id+"F0.wireOp",EDGE,"E8.bottom"),subQ10,subQ9,sQuery(id+"F0.wireOp",EDGE,"E8.right"),subQ8,sQuery(id+"F0.wireOp",EDGE,"E12.top"),subQ7,sQuery(id+"F0.wireOp",EDGE,"E27.top"),sQuery(id+"F0.wireOp",EDGE,"E27.right"),subQ6])],"isStart":true}),makeQuery(id+"F2.opExtrude","CAP_FACE",FACE,{"disambiguationData":[OSD([subQ5,sQuery(id+"F0.wireOp",EDGE,"E21.top"),sQuery(id+"F0.wireOp",EDGE,"E21.right"),subQ4,sQuery(id+"F0.wireOp",EDGE,"E29.top"),subQ3,sQuery(id+"F0.wireOp",EDGE,"E29.right")])],"isStart":true}),makeQuery(id+"F2.opExtrude","CAP_FACE",FACE,{"disambiguationData":[OSD([sQuery(id+"F0.wireOp",EDGE,"E22.bottom"),subQ2,sQuery(id+"F0.wireOp",EDGE,"E22.right"),subQ1,sQuery(id+"F0.wireOp",EDGE,"E25.top"),subQ0,sQuery(id+"F0.wireOp",EDGE,"E25.right")])],"isStart":true})]})]});}
            var Q6;
            Q6=makeQuery(id+"F2.opExtrude","CAP_EDGE",EDGE,{"disambiguationData":[OSD([sQuery(id+"F0.wireOp",EDGE,"E9.top")])],"isStart":true});
            var Q7;
            Q7=makeQuery(id+"F2.opExtrude","CAP_EDGE",EDGE,{"disambiguationData":[OSD([sQuery(id+"F0.wireOp",EDGE,"E6.right")])],"isStart":true});
            var Q8;
            {var subQ0=sQuery(id+"F0.wireOp",EDGE,"E24.right");var subQ1=sQuery(id+"F0.wireOp",EDGE,"E25.bottom");var subQ2=sQuery(id+"F0.wireOp",EDGE,"E22.top");var subQ3=sQuery(id+"F0.wireOp",EDGE,"E28.right");var subQ4=sQuery(id+"F0.wireOp",EDGE,"E29.bottom");var subQ5=sQuery(id+"F0.wireOp",EDGE,"E21.bottom");var subQ6=sQuery(id+"F0.wireOp",EDGE,"E27.left");var subQ7=sQuery(id+"F0.wireOp",EDGE,"E27.bottom");var subQ8=sQuery(id+"F0.wireOp",EDGE,"E12.bottom");var subQ9=sQuery(id+"F0.wireOp",EDGE,"E2");var subQ10=sQuery(id+"F0.wireOp",EDGE,"E8.top");var subQ11=sQuery(id+"F0.wireOp",EDGE,"E14.bottom");var subQ12=sQuery(id+"F0.wireOp",EDGE,"E13.bottom");var subQ13=sQuery(id+"F0.wireOp",EDGE,"E18.bottom");var subQ14=sQuery(id+"F0.wireOp",EDGE,"E17.bottom");var subQ15=sQuery(id+"F0.wireOp",EDGE,"E11.bottom");var subQ16=sQuery(id+"F0.wireOp",EDGE,"E10.bottom");var subQ17=sQuery(id+"F0.wireOp",EDGE,"E4");var subQ18=sQuery(id+"F0.wireOp",EDGE,"E7.top");var subQ19=sQuery(id+"F0.wireOp",EDGE,"E7.bottom");var subQ20=sQuery(id+"F0.wireOp",EDGE,"E24.left");var subQ21=sQuery(id+"F0.wireOp",EDGE,"E26.bottom");var subQ22=sQuery(id+"F0.wireOp",EDGE,"E9.top");var subQ23=sQuery(id+"F0.wireOp",EDGE,"E9.bottom");var subQ24=sQuery(id+"F0.wireOp",EDGE,"E6.right");var subQ25=sQuery(id+"F0.wireOp",EDGE,"E6.left");var subQ26=sQuery(id+"F0.wireOp",EDGE,"E6.top");var subQ27=sQuery(id+"F0.wireOp",EDGE,"E5.left");Q8=makeQuery(id+"F3.opFillet","BLEND_EDGE",EDGE,{"blendedFrom":[makeQuery(id+"F2.opExtrude","SWEPT_EDGE",EDGE,{"disambiguationData":[OSD([subQ24,subQ22,sQuery(id+"F0.wireOp",EDGE,"E9.left")])]}),makeQuery(id+"F2.boolean.opBoolean","MERGE",FACE,{"derivedFrom":[makeQuery(id+"F1.opExtrude","CAP_FACE",FACE,{"disambiguationData":[OSD([sQuery(id+"F0.wireOp",EDGE,"E0.bottom"),sQuery(id+"F0.wireOp",EDGE,"E0.top"),sQuery(id+"F0.wireOp",EDGE,"E1.right"),sQuery(id+"F0.wireOp",EDGE,"E3.right"),subQ27,subQ26,subQ25,subQ19,subQ18,subQ17,subQ10,subQ9,subQ23,subQ16,subQ15,subQ8,subQ14,subQ13,subQ5,subQ2,sQuery(id+"F0.wireOp",EDGE,"E24.top"),subQ1,subQ0,subQ21,subQ20,subQ7,sQuery(id+"F0.wireOp",EDGE,"E28.top"),subQ6,subQ4,subQ3,subQ12,subQ11])],"isStart":true}),makeQuery(id+"F2.opExtrude","CAP_FACE",FACE,{"disambiguationData":[OSD([sQuery(id+"F0.wireOp",EDGE,"E5.bottom"),sQuery(id+"F0.wireOp",EDGE,"E5.top"),subQ27,sQuery(id+"F0.wireOp",EDGE,"E5.right")])],"isStart":true}),makeQuery(id+"F2.opExtrude","CAP_FACE",FACE,{"disambiguationData":[OSD([sQuery(id+"F0.wireOp",EDGE,"E6.bottom"),subQ26,subQ25,subQ24,subQ23,subQ22,subQ21,sQuery(id+"F0.wireOp",EDGE,"E26.top"),subQ20,sQuery(id+"F0.wireOp",EDGE,"E26.right")])],"isStart":true}),makeQuery(id+"F2.opExtrude","CAP_FACE",FACE,{"disambiguationData":[OSD([subQ19,subQ18,subQ17,sQuery(id+"F0.wireOp",EDGE,"E7.right"),subQ16,sQuery(id+"F0.wireOp",EDGE,"E10.top"),subQ15,sQuery(id+"F0.wireOp",EDGE,"E11.top"),sQuery(id+"F0.wireOp",EDGE,"E15.bottom"),sQuery(id+"F0.wireOp",EDGE,"E16.bottom"),subQ14,sQuery(id+"F0.wireOp",EDGE,"E17.top"),sQuery(id+"F0.wireOp",EDGE,"E17.right"),subQ13,sQuery(id+"F0.wireOp",EDGE,"E18.top"),sQuery(id+"F0.wireOp",EDGE,"E18.right"),sQuery(id+"F0.wireOp",EDGE,"E19.bottom"),sQuery(id+"F0.wireOp",EDGE,"E20.bottom"),subQ12,sQuery(id+"F0.wireOp",EDGE,"E30.top"),sQuery(id+"F0.wireOp",EDGE,"E31.bottom"),subQ11])],"isStart":true}),makeQuery(id+"F2.opExtrude","CAP_FACE",FACE,{"disambiguationData":[OSD([sQuery(id+"F0.wireOp",EDGE,"E8.bottom"),subQ10,subQ9,sQuery(id+"F0.wireOp",EDGE,"E8.right"),subQ8,sQuery(id+"F0.wireOp",EDGE,"E12.top"),subQ7,sQuery(id+"F0.wireOp",EDGE,"E27.top"),sQuery(id+"F0.wireOp",EDGE,"E27.right"),subQ6])],"isStart":true}),makeQuery(id+"F2.opExtrude","CAP_FACE",FACE,{"disambiguationData":[OSD([subQ5,sQuery(id+"F0.wireOp",EDGE,"E21.top"),sQuery(id+"F0.wireOp",EDGE,"E21.right"),subQ4,sQuery(id+"F0.wireOp",EDGE,"E29.top"),subQ3,sQuery(id+"F0.wireOp",EDGE,"E29.right")])],"isStart":true}),makeQuery(id+"F2.opExtrude","CAP_FACE",FACE,{"disambiguationData":[OSD([sQuery(id+"F0.wireOp",EDGE,"E22.bottom"),subQ2,sQuery(id+"F0.wireOp",EDGE,"E22.right"),subQ1,sQuery(id+"F0.wireOp",EDGE,"E25.top"),subQ0,sQuery(id+"F0.wireOp",EDGE,"E25.right")])],"isStart":true})]})],"blendedInto":[makeQuery(id+"F2.boolean.opBoolean","MERGE",FACE,{"derivedFrom":[makeQuery(id+"F1.opExtrude","CAP_FACE",FACE,{"disambiguationData":[OSD([sQuery(id+"F0.wireOp",EDGE,"E0.bottom"),sQuery(id+"F0.wireOp",EDGE,"E0.top"),sQuery(id+"F0.wireOp",EDGE,"E1.right"),sQuery(id+"F0.wireOp",EDGE,"E3.right"),subQ27,subQ26,subQ25,subQ19,subQ18,subQ17,subQ10,subQ9,subQ23,subQ16,subQ15,subQ8,subQ14,subQ13,subQ5,subQ2,sQuery(id+"F0.wireOp",EDGE,"E24.top"),subQ1,subQ0,subQ21,subQ20,subQ7,sQuery(id+"F0.wireOp",EDGE,"E28.top"),subQ6,subQ4,subQ3,subQ12,subQ11])],"isStart":true}),makeQuery(id+"F2.opExtrude","CAP_FACE",FACE,{"disambiguationData":[OSD([sQuery(id+"F0.wireOp",EDGE,"E5.bottom"),sQuery(id+"F0.wireOp",EDGE,"E5.top"),subQ27,sQuery(id+"F0.wireOp",EDGE,"E5.right")])],"isStart":true}),makeQuery(id+"F2.opExtrude","CAP_FACE",FACE,{"disambiguationData":[OSD([sQuery(id+"F0.wireOp",EDGE,"E6.bottom"),subQ26,subQ25,subQ24,subQ23,subQ22,subQ21,sQuery(id+"F0.wireOp",EDGE,"E26.top"),subQ20,sQuery(id+"F0.wireOp",EDGE,"E26.right")])],"isStart":true}),makeQuery(id+"F2.opExtrude","CAP_FACE",FACE,{"disambiguationData":[OSD([subQ19,subQ18,subQ17,sQuery(id+"F0.wireOp",EDGE,"E7.right"),subQ16,sQuery(id+"F0.wireOp",EDGE,"E10.top"),subQ15,sQuery(id+"F0.wireOp",EDGE,"E11.top"),sQuery(id+"F0.wireOp",EDGE,"E15.bottom"),sQuery(id+"F0.wireOp",EDGE,"E16.bottom"),subQ14,sQuery(id+"F0.wireOp",EDGE,"E17.top"),sQuery(id+"F0.wireOp",EDGE,"E17.right"),subQ13,sQuery(id+"F0.wireOp",EDGE,"E18.top"),sQuery(id+"F0.wireOp",EDGE,"E18.right"),sQuery(id+"F0.wireOp",EDGE,"E19.bottom"),sQuery(id+"F0.wireOp",EDGE,"E20.bottom"),subQ12,sQuery(id+"F0.wireOp",EDGE,"E30.top"),sQuery(id+"F0.wireOp",EDGE,"E31.bottom"),subQ11])],"isStart":true}),makeQuery(id+"F2.opExtrude","CAP_FACE",FACE,{"disambiguationData":[OSD([sQuery(id+"F0.wireOp",EDGE,"E8.bottom"),subQ10,subQ9,sQuery(id+"F0.wireOp",EDGE,"E8.right"),subQ8,sQuery(id+"F0.wireOp",EDGE,"E12.top"),subQ7,sQuery(id+"F0.wireOp",EDGE,"E27.top"),sQuery(id+"F0.wireOp",EDGE,"E27.right"),subQ6])],"isStart":true}),makeQuery(id+"F2.opExtrude","CAP_FACE",FACE,{"disambiguationData":[OSD([subQ5,sQuery(id+"F0.wireOp",EDGE,"E21.top"),sQuery(id+"F0.wireOp",EDGE,"E21.right"),subQ4,sQuery(id+"F0.wireOp",EDGE,"E29.top"),subQ3,sQuery(id+"F0.wireOp",EDGE,"E29.right")])],"isStart":true}),makeQuery(id+"F2.opExtrude","CAP_FACE",FACE,{"disambiguationData":[OSD([sQuery(id+"F0.wireOp",EDGE,"E22.bottom"),subQ2,sQuery(id+"F0.wireOp",EDGE,"E22.right"),subQ1,sQuery(id+"F0.wireOp",EDGE,"E25.top"),subQ0,sQuery(id+"F0.wireOp",EDGE,"E25.right")])],"isStart":true})]})]});}
            var Q9;
            Q9=makeQuery(id+"F2.opExtrude","CAP_EDGE",EDGE,{"disambiguationData":[OSD([sQuery(id+"F0.wireOp",EDGE,"E12.top")])],"isStart":true});
            var Q10;
            Q10=makeQuery(id+"F2.opExtrude","CAP_EDGE",EDGE,{"disambiguationData":[OSD([sQuery(id+"F0.wireOp",EDGE,"E21.top")])],"isStart":true});
            var Q11;
            Q11=makeQuery(id+"F2.opExtrude","CAP_EDGE",EDGE,{"disambiguationData":[OSD([sQuery(id+"F0.wireOp",EDGE,"E5.right")])],"isStart":true});
            fillet(context, id + "F4", {"entities" : qUnion([Q0, Q1, Q2, Q3, Q4, Q5, Q6, Q7, Q8, Q9, Q10, Q11]), "radius" : .5 * mm, "tangentPropagation" : true, "allowEdgeOverflow" : false});
        }
    });
